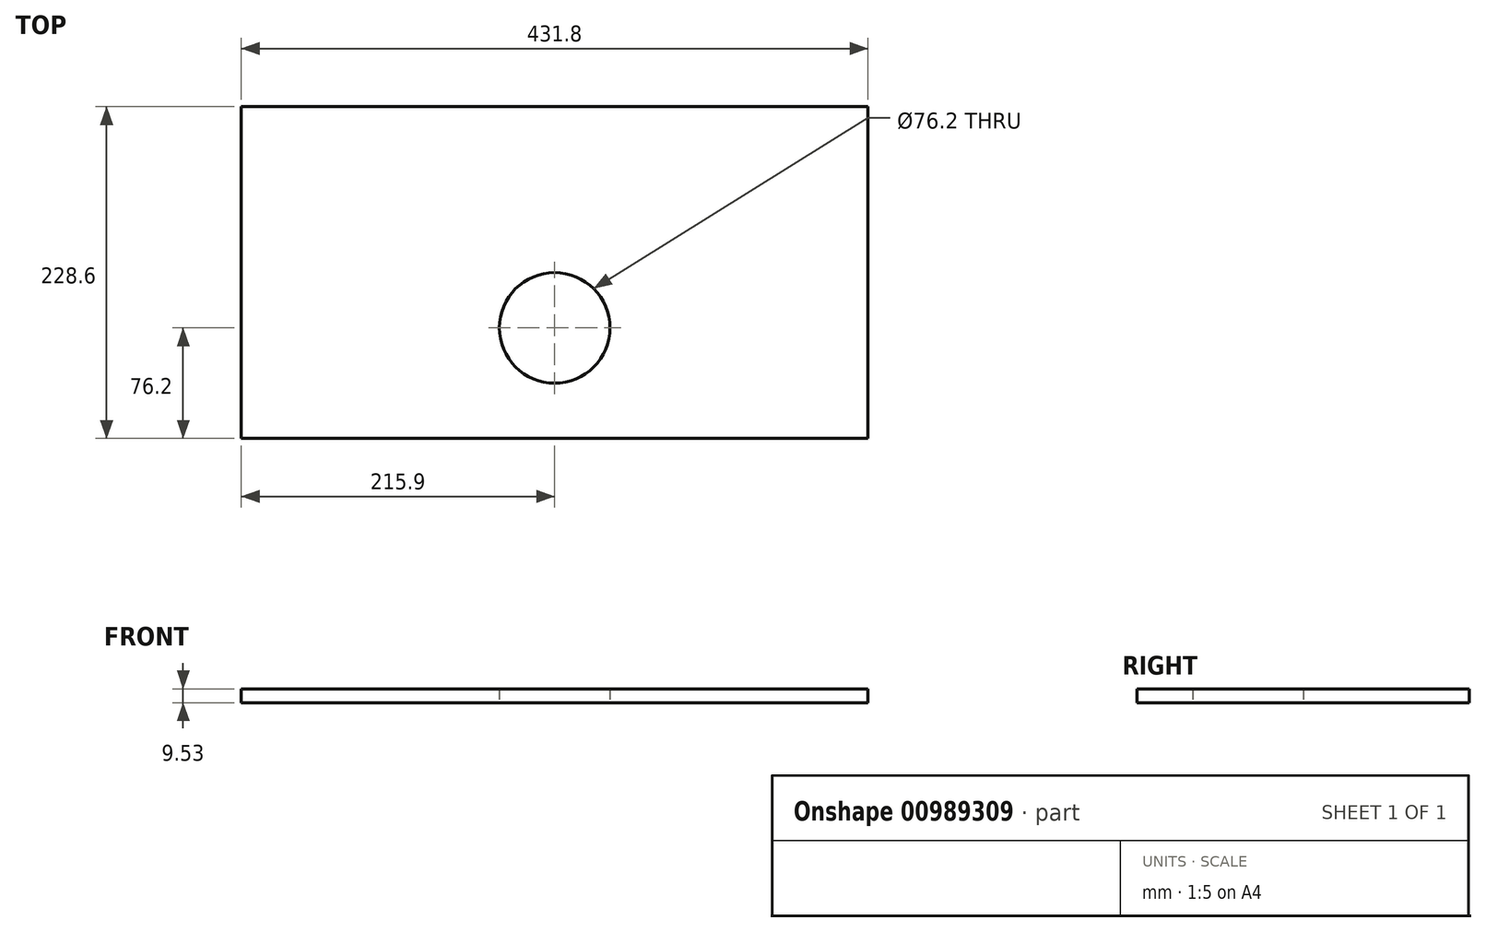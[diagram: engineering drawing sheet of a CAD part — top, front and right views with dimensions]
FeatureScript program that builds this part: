
annotation { "Feature Type Name" : "Feature", "Feature Type Description" : "" }
export const myFeature = defineFeature(function(context is Context, id is Id, definition is map)
    precondition{}
    {
        {
            var Q0;
            Q0=qCreatedBy(makeId("Top.planeOp"),FACE);
            var sketch = newSketch(context, id + "F0", { "sketchPlane" : qUnion([Q0])});
            skLineSegment(sketch, "E0.bottom", {"start": v(0, 0) * mm, "end": v(431.8, 0) * mm});
            skLineSegment(sketch, "E0.top", {"start": v(0, 228.6) * mm, "end": v(431.8, 228.6) * mm});
            skLineSegment(sketch, "E0.left", {"start": v(0, 0) * mm, "end": v(0, 228.6) * mm});
            skLineSegment(sketch, "E0.right", {"start": v(431.8, 0) * mm, "end": v(431.8, 228.6) * mm});
            skCircle(sketch, "E1", {"center": v(215.9, 76.2) * mm, "radius": 38.1 * mm});
            skSolve(sketch);
        }
        {
            var Q0;
            Q0=makeQuery(id+"F0.imprint","IMPRINT",FACE,{"disambiguationData":[TD([[makeQuery(id+"F0.imprint","IMPRINT",EDGE,{"derivedFrom":sQuery(id+"F0.wireOp",EDGE,"E0.bottom")}),1.0]])]});
            extrude(context, id + "F1", {"entities" : qUnion([Q0]), "depth" : 9.52 * mm, "offsetDistance" : 25.4 * mm});
        }
    });
